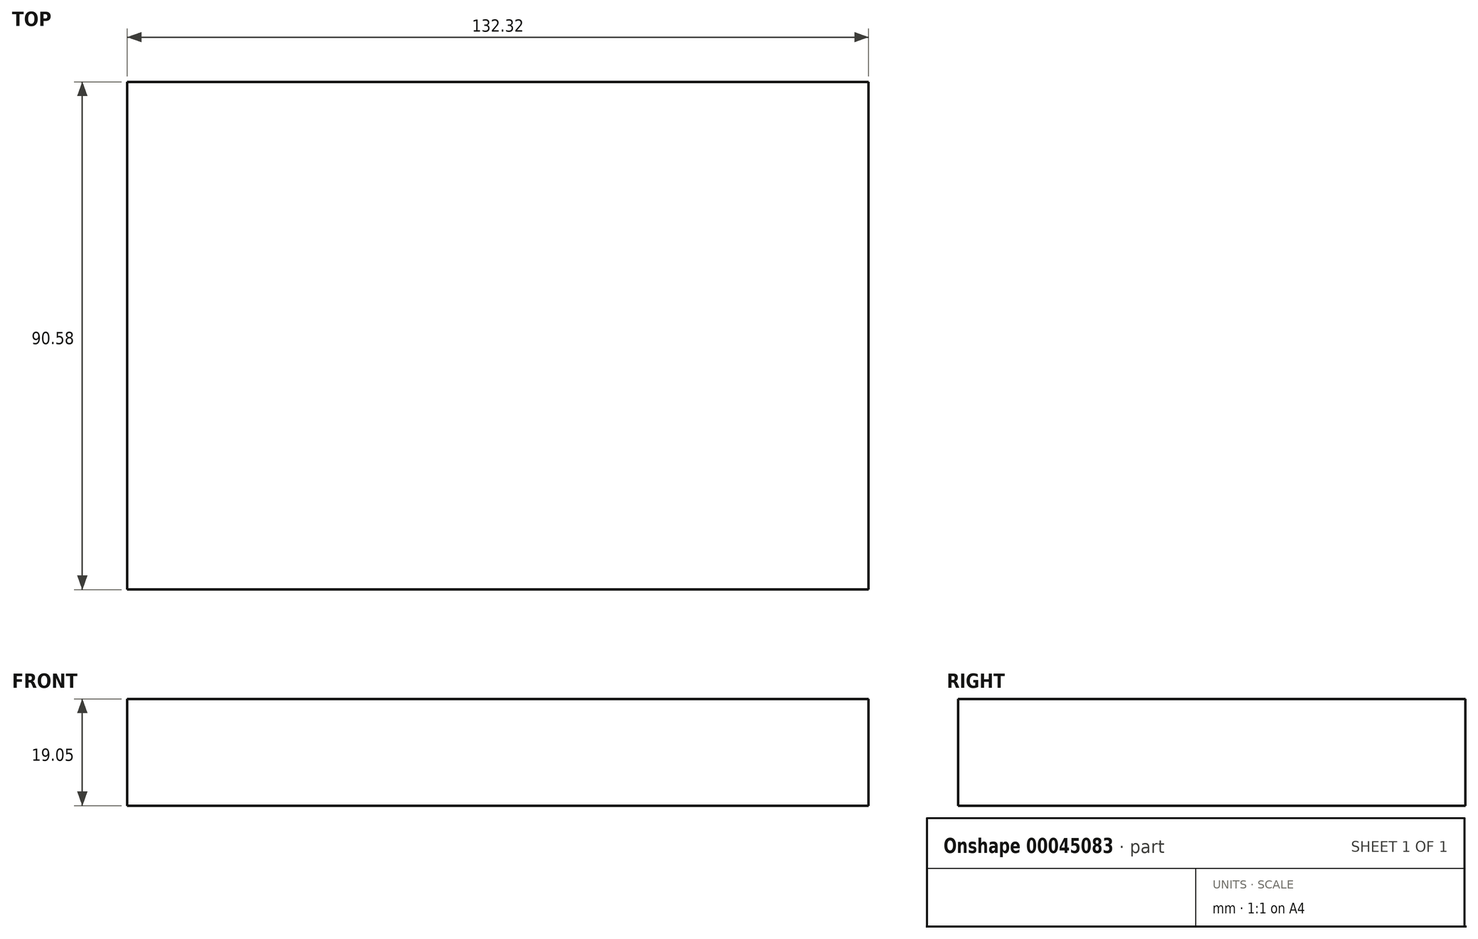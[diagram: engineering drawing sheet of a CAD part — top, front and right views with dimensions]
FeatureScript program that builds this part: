
annotation { "Feature Type Name" : "Feature", "Feature Type Description" : "" }
export const myFeature = defineFeature(function(context is Context, id is Id, definition is map)
    precondition{}
    {
        {
            var Q0;
            Q0=qCreatedBy(makeId("Top.planeOp"),FACE);
            var sketch = newSketch(context, id + "F0", { "sketchPlane" : qUnion([Q0])});
            skLineSegment(sketch, "E0.rect.bottom", {"start": v(-66.16, 45.29) * mm, "end": v(66.16, 45.29) * mm});
            skLineSegment(sketch, "E0.rect.top", {"start": v(-66.16, -45.29) * mm, "end": v(66.16, -45.29) * mm});
            skLineSegment(sketch, "E0.rect.left", {"start": v(-66.16, 45.29) * mm, "end": v(-66.16, -45.29) * mm});
            skLineSegment(sketch, "E0.rect.right", {"start": v(66.16, 45.29) * mm, "end": v(66.16, -45.29) * mm});
            skPoint(sketch, "E0.rect.middle", {"position": v(0, 0) * mm});
            skSolve(sketch);
        }
        {
            var Q0;
            Q0 = qSketchRegion(id + "F0", true);
            extrude(context, id + "F1", {"entities" : qUnion([Q0]), "depth" : 19.05 * mm});
        }
    });
